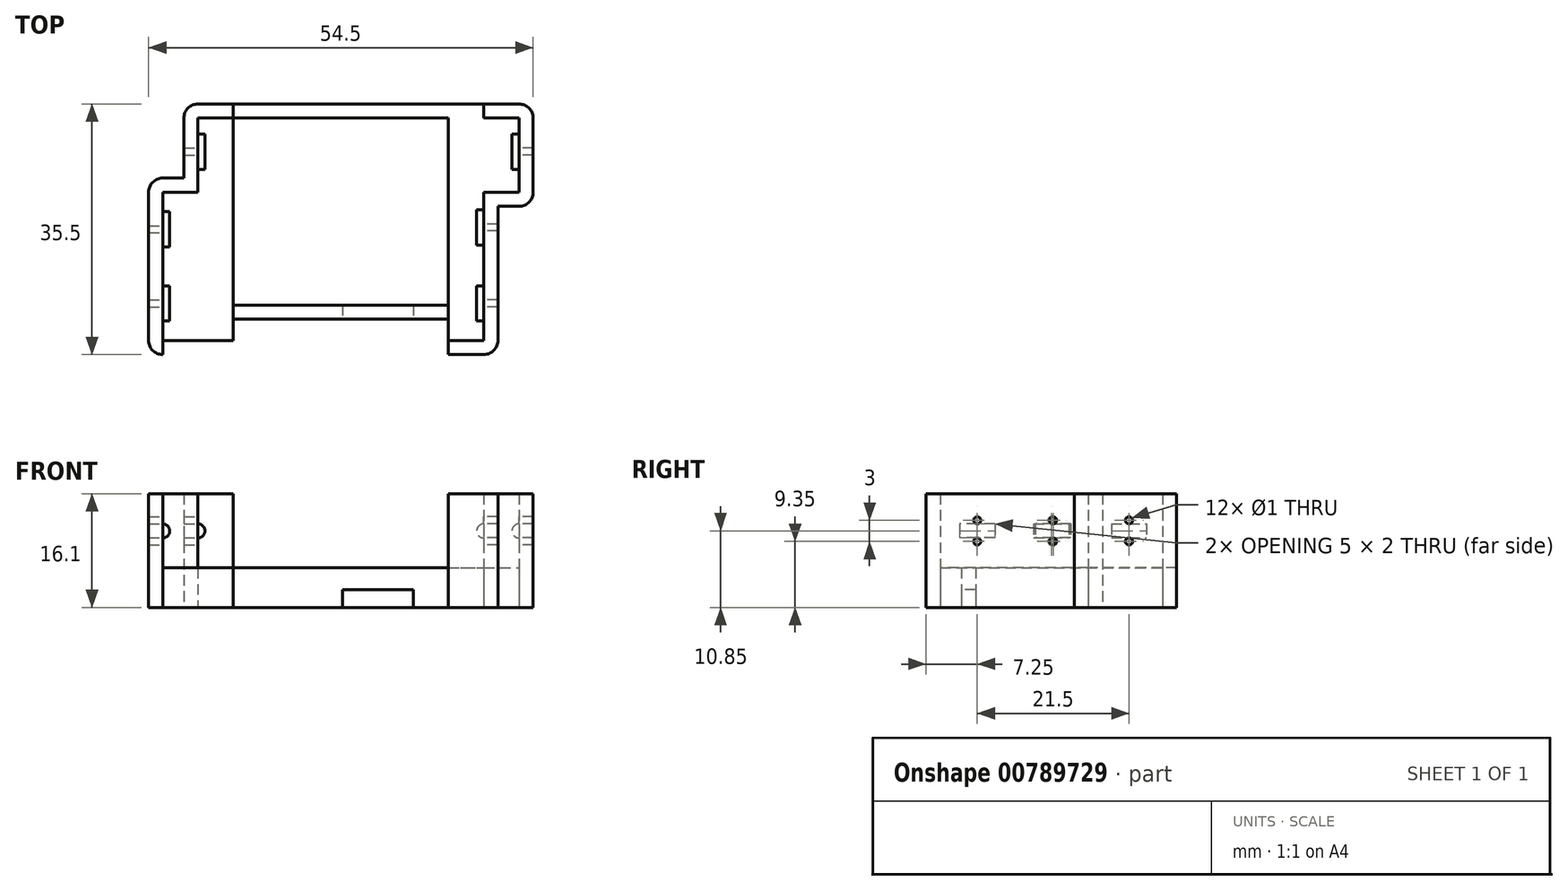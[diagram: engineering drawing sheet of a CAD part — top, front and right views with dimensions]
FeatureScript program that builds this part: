
annotation { "Feature Type Name" : "Feature", "Feature Type Description" : "" }
export const myFeature = defineFeature(function(context is Context, id is Id, definition is map)
    precondition{}
    {
        {
            var Q0;
            Q0=qCreatedBy(makeId("Top.planeOp"),FACE);
            var sketch = newSketch(context, id + "F0", { "sketchPlane" : qUnion([Q0])});
            skLineSegment(sketch, "E0", {"start": v(0, 0) * mm, "end": v(0, 23) * mm});
            skLineSegment(sketch, "E1", {"start": v(0, 23) * mm, "end": v(5, 23) * mm});
            skLineSegment(sketch, "E2", {"start": v(5, 23) * mm, "end": v(5, 35.5) * mm});
            skLineSegment(sketch, "E3", {"start": v(5, 35.5) * mm, "end": v(54.5, 35.5) * mm});
            skLineSegment(sketch, "E4", {"start": v(54.5, 35.5) * mm, "end": v(54.5, 23) * mm});
            skLineSegment(sketch, "E5", {"start": v(54.5, 23) * mm, "end": v(49.5, 23) * mm});
            skLineSegment(sketch, "E6", {"start": v(49.5, 23) * mm, "end": v(49.5, 0) * mm});
            skLineSegment(sketch, "E7", {"start": v(49.5, 0) * mm, "end": v(0, 0) * mm});
            skLineSegment(sketch, "E8", {"start": v(5, 33.5) * mm, "end": v(54.5, 33.5) * mm});
            skLineSegment(sketch, "E9", {"start": v(5, 23) * mm, "end": v(49.5, 23) * mm});
            skLineSegment(sketch, "E10", {"start": v(7, 35.5) * mm, "end": v(7, 0) * mm});
            skLineSegment(sketch, "E11", {"start": v(2, 0) * mm, "end": v(2, 23) * mm});
            skLineSegment(sketch, "E12", {"start": v(0, 2) * mm, "end": v(49.5, 2) * mm});
            skLineSegment(sketch, "E13", {"start": v(47.5, 23) * mm, "end": v(47.5, 0) * mm});
            skLineSegment(sketch, "E14", {"start": v(52.5, 35.5) * mm, "end": v(52.5, 23) * mm});
            skLineSegment(sketch, "E15", {"start": v(12, 35.5) * mm, "end": v(12, 0) * mm});
            skLineSegment(sketch, "E16", {"start": v(0, 23) * mm, "end": v(0, 25) * mm});
            skLineSegment(sketch, "E17", {"start": v(0, 25) * mm, "end": v(5, 25) * mm});
            skLineSegment(sketch, "E18", {"start": v(54.5, 23) * mm, "end": v(54.5, 21) * mm});
            skLineSegment(sketch, "E19", {"start": v(54.5, 21) * mm, "end": v(49.5, 21) * mm});
            skLineSegment(sketch, "E20", {"start": v(7, 0) * mm, "end": v(7, 2) * mm});
            skLineSegment(sketch, "E21", {"start": v(42.5, 0) * mm, "end": v(42.5, 35.5) * mm});
            skLineSegment(sketch, "E22", {"start": v(47.5, 35.5) * mm, "end": v(47.5, 33.5) * mm});
            skLineSegment(sketch, "E23", {"start": v(12, 5) * mm, "end": v(42.5, 5) * mm});
            skLineSegment(sketch, "E24", {"start": v(42.5, 7) * mm, "end": v(12, 7) * mm});
            skSolve(sketch);
        }
        {
            var Q0;
            {var subQ1=sQuery(id+"F0.wireOp",EDGE,"E4");var subQ3=sQuery(id+"F0.wireOp",EDGE,"E8");var subQ4=makeQuery(id+"F0.imprint","INTERSECT",VERTEX,{"derivedFrom":[subQ1,subQ3]});Q0=makeQuery(id+"F0.imprint","IMPRINT",FACE,{"disambiguationData":[TD([[makeQuery(id+"F0.imprint","IMPRINT",EDGE,{"disambiguationData":[TD([[subQ4,1.0]])],"derivedFrom":subQ3}),-1.0]])]});}
            var Q1;
            {var subQ0=sQuery(id+"F0.wireOp",EDGE,"E4");var subQ1=sQuery(id+"F0.wireOp",EDGE,"E3");var subQ2=makeQuery(id+"F0.imprint","INTERSECT",VERTEX,{"derivedFrom":[subQ1,subQ0]});Q1=makeQuery(id+"F0.imprint","IMPRINT",FACE,{"disambiguationData":[TD([[makeQuery(id+"F0.imprint","IMPRINT",EDGE,{"disambiguationData":[TD([[subQ2,1.0]])],"derivedFrom":subQ1}),-1.0]])]});}
            var Q2;
            {var subQ0=sQuery(id+"F0.wireOp",EDGE,"E18");Q2=makeQuery(id+"F0.imprint","IMPRINT",FACE,{"disambiguationData":[TD([[makeQuery(id+"F0.imprint","IMPRINT",EDGE,{"derivedFrom":subQ0}),-1.0]])]});}
            var Q3;
            {var subQ0=sQuery(id+"F0.wireOp",EDGE,"E12");var subQ1=sQuery(id+"F0.wireOp",EDGE,"E6");var subQ2=makeQuery(id+"F0.imprint","INTERSECT",VERTEX,{"derivedFrom":[subQ1,subQ0]});Q3=makeQuery(id+"F0.imprint","IMPRINT",FACE,{"disambiguationData":[TD([[makeQuery(id+"F0.imprint","IMPRINT",EDGE,{"disambiguationData":[TD([[subQ2,1.0]])],"derivedFrom":subQ1}),-1.0]])]});}
            var Q4;
            {var subQ0=sQuery(id+"F0.wireOp",EDGE,"E7");var subQ1=sQuery(id+"F0.wireOp",EDGE,"E6");var subQ2=makeQuery(id+"F0.imprint","INTERSECT",VERTEX,{"derivedFrom":[subQ1,subQ0]});Q4=makeQuery(id+"F0.imprint","IMPRINT",FACE,{"disambiguationData":[TD([[makeQuery(id+"F0.imprint","IMPRINT",EDGE,{"disambiguationData":[TD([[subQ2,1.0]])],"derivedFrom":subQ1}),-1.0]])]});}
            var Q5;
            {var subQ0=sQuery(id+"F0.wireOp",EDGE,"E3");var subQ1=sQuery(id+"F0.wireOp",EDGE,"E2");var subQ2=makeQuery(id+"F0.imprint","INTERSECT",VERTEX,{"derivedFrom":[subQ1,subQ0]});Q5=makeQuery(id+"F0.imprint","IMPRINT",FACE,{"disambiguationData":[TD([[makeQuery(id+"F0.imprint","IMPRINT",EDGE,{"disambiguationData":[TD([[subQ2,1.0]])],"derivedFrom":subQ1}),-1.0]])]});}
            var Q6;
            {var subQ1=sQuery(id+"F0.wireOp",EDGE,"E2");var subQ5=sQuery(id+"F0.wireOp",EDGE,"E8");var subQ6=makeQuery(id+"F0.imprint","INTERSECT",VERTEX,{"derivedFrom":[subQ1,subQ5]});Q6=makeQuery(id+"F0.imprint","IMPRINT",FACE,{"disambiguationData":[TD([[makeQuery(id+"F0.imprint","IMPRINT",EDGE,{"disambiguationData":[TD([[subQ6,1.0]])],"derivedFrom":subQ1}),-1.0]])]});}
            var Q7;
            {var subQ0=sQuery(id+"F0.wireOp",EDGE,"E16");Q7=makeQuery(id+"F0.imprint","IMPRINT",FACE,{"disambiguationData":[TD([[makeQuery(id+"F0.imprint","IMPRINT",EDGE,{"derivedFrom":subQ0}),-1.0]])]});}
            var Q8;
            {var subQ0=sQuery(id+"F0.wireOp",EDGE,"E1");var subQ5=sQuery(id+"F0.wireOp",EDGE,"E11");var subQ6=makeQuery(id+"F0.imprint","INTERSECT",VERTEX,{"derivedFrom":[subQ0,subQ5]});Q8=makeQuery(id+"F0.imprint","IMPRINT",FACE,{"disambiguationData":[TD([[makeQuery(id+"F0.imprint","IMPRINT",EDGE,{"disambiguationData":[TD([[subQ6,1.0]])],"derivedFrom":subQ5}),1.0]])]});}
            var Q9;
            {var subQ0=sQuery(id+"F0.wireOp",EDGE,"E7");var subQ1=sQuery(id+"F0.wireOp",EDGE,"E0");var subQ2=makeQuery(id+"F0.imprint","INTERSECT",VERTEX,{"derivedFrom":[subQ1,subQ0]});Q9=makeQuery(id+"F0.imprint","IMPRINT",FACE,{"disambiguationData":[TD([[makeQuery(id+"F0.imprint","IMPRINT",EDGE,{"disambiguationData":[TD([[subQ2,-1.0]])],"derivedFrom":subQ1}),-1.0]])]});}
            var Q10;
            {var subQ3=sQuery(id+"F0.wireOp",EDGE,"E20");Q10=makeQuery(id+"F0.imprint","IMPRINT",FACE,{"disambiguationData":[TD([[makeQuery(id+"F0.imprint","IMPRINT",EDGE,{"derivedFrom":subQ3}),1.0]])]});}
            var Q11;
            {var subQ0=sQuery(id+"F0.wireOp",EDGE,"E13");var subQ1=sQuery(id+"F0.wireOp",EDGE,"E7");var subQ2=makeQuery(id+"F0.imprint","INTERSECT",VERTEX,{"derivedFrom":[subQ1,subQ0]});Q11=makeQuery(id+"F0.imprint","IMPRINT",FACE,{"disambiguationData":[TD([[makeQuery(id+"F0.imprint","IMPRINT",EDGE,{"disambiguationData":[TD([[subQ2,-1.0]])],"derivedFrom":subQ1}),-1.0]])]});}
            var Q12;
            {var subQ0=sQuery(id+"F0.wireOp",EDGE,"E10");var subQ1=sQuery(id+"F0.wireOp",EDGE,"E3");var subQ2=makeQuery(id+"F0.imprint","INTERSECT",VERTEX,{"derivedFrom":[subQ1,subQ0]});Q12=makeQuery(id+"F0.imprint","IMPRINT",FACE,{"disambiguationData":[TD([[makeQuery(id+"F0.imprint","IMPRINT",EDGE,{"disambiguationData":[TD([[subQ2,-1.0]])],"derivedFrom":subQ1}),-1.0]])]});}
            var Q13;
            {var subQ3=sQuery(id+"F0.wireOp",EDGE,"E22");Q13=makeQuery(id+"F0.imprint","IMPRINT",FACE,{"disambiguationData":[TD([[makeQuery(id+"F0.imprint","IMPRINT",EDGE,{"derivedFrom":subQ3}),1.0]])]});}
            extrude(context, id + "F1", {"entities" : qUnion([Q0, Q1, Q2, Q3, Q4, Q5, Q6, Q7, Q8, Q9, Q10, Q11, Q12, Q13]), "depth" : 16.1 * mm, "offsetDistance" : 25 * mm});
        }
        {
            var Q0;
            {var subQ0=sQuery(id+"F0.wireOp",EDGE,"E15");var subQ1=sQuery(id+"F0.wireOp",EDGE,"E3");var subQ2=makeQuery(id+"F0.imprint","INTERSECT",VERTEX,{"derivedFrom":[subQ1,subQ0]});Q0=makeQuery(id+"F0.imprint","IMPRINT",FACE,{"disambiguationData":[TD([[makeQuery(id+"F0.imprint","IMPRINT",EDGE,{"disambiguationData":[TD([[subQ2,-1.0]])],"derivedFrom":subQ1}),-1.0]])]});}
            var Q1;
            {var subQ3=sQuery(id+"F0.wireOp",EDGE,"E22");Q1=makeQuery(id+"F0.imprint","IMPRINT",FACE,{"disambiguationData":[TD([[makeQuery(id+"F0.imprint","IMPRINT",EDGE,{"derivedFrom":subQ3}),-1.0]])]});}
            var Q2;
            {var subQ3=sQuery(id+"F0.wireOp",EDGE,"E20");Q2=makeQuery(id+"F0.imprint","IMPRINT",FACE,{"disambiguationData":[TD([[makeQuery(id+"F0.imprint","IMPRINT",EDGE,{"derivedFrom":subQ3}),-1.0]])]});}
            var Q3;
            {var subQ0=sQuery(id+"F0.wireOp",EDGE,"E11");var subQ1=sQuery(id+"F0.wireOp",EDGE,"E1");var subQ2=makeQuery(id+"F0.imprint","INTERSECT",VERTEX,{"derivedFrom":[subQ1,subQ0]});Q3=makeQuery(id+"F0.imprint","IMPRINT",FACE,{"disambiguationData":[TD([[makeQuery(id+"F0.imprint","IMPRINT",EDGE,{"disambiguationData":[TD([[subQ2,1.0]])],"derivedFrom":subQ0}),-1.0]])]});}
            var Q4;
            {var subQ0=sQuery(id+"F0.wireOp",EDGE,"E10");var subQ1=sQuery(id+"F0.wireOp",EDGE,"E9");var subQ2=makeQuery(id+"F0.imprint","INTERSECT",VERTEX,{"derivedFrom":[subQ1,subQ0]});Q4=makeQuery(id+"F0.imprint","IMPRINT",FACE,{"disambiguationData":[TD([[makeQuery(id+"F0.imprint","IMPRINT",EDGE,{"disambiguationData":[TD([[subQ2,-1.0]])],"derivedFrom":subQ1}),-1.0]])]});}
            var Q5;
            {var subQ0=sQuery(id+"F0.wireOp",EDGE,"E10");var subQ1=sQuery(id+"F0.wireOp",EDGE,"E8");var subQ2=makeQuery(id+"F0.imprint","INTERSECT",VERTEX,{"derivedFrom":[subQ1,subQ0]});Q5=makeQuery(id+"F0.imprint","IMPRINT",FACE,{"disambiguationData":[TD([[makeQuery(id+"F0.imprint","IMPRINT",EDGE,{"disambiguationData":[TD([[subQ2,-1.0]])],"derivedFrom":subQ1}),-1.0]])]});}
            var Q6;
            {var subQ4=sQuery(id+"F0.wireOp",EDGE,"E8");var subQ5=makeQuery(id+"F0.imprint","INTERSECT",VERTEX,{"derivedFrom":[subQ4,sQuery(id+"F0.wireOp",EDGE,"E22")]});Q6=makeQuery(id+"F0.imprint","IMPRINT",FACE,{"disambiguationData":[TD([[makeQuery(id+"F0.imprint","IMPRINT",EDGE,{"disambiguationData":[TD([[subQ5,1.0]])],"derivedFrom":subQ4}),-1.0]])]});}
            var Q7;
            {var subQ0=sQuery(id+"F0.wireOp",EDGE,"E13");var subQ1=sQuery(id+"F0.wireOp",EDGE,"E9");var subQ2=makeQuery(id+"F0.imprint","INTERSECT",VERTEX,{"derivedFrom":[subQ1,subQ0]});Q7=makeQuery(id+"F0.imprint","IMPRINT",FACE,{"disambiguationData":[TD([[makeQuery(id+"F0.imprint","IMPRINT",EDGE,{"disambiguationData":[TD([[subQ2,1.0]])],"derivedFrom":subQ1}),-1.0]])]});}
            extrude(context, id + "F2", {"entities" : qUnion([Q0, Q1, Q2, Q3, Q4, Q5, Q6, Q7]), "depth" : 5.6 * mm, "offsetDistance" : 25 * mm});
        }
        {
            var Q0;
            {var subQ0=sQuery(id+"F0.wireOp",EDGE,"E23");Q0=makeQuery(id+"F0.imprint","IMPRINT",FACE,{"disambiguationData":[TD([[makeQuery(id+"F0.imprint","IMPRINT",EDGE,{"derivedFrom":subQ0}),1.0]])]});}
            extrude(context, id + "F3", {"entities" : qUnion([Q0]), "depth" : 5.6 * mm, "offsetDistance" : 25 * mm});
        }
        {
            var Q0;
            Q0=makeQuery(id+"F1.opExtrude","SWEPT_EDGE",EDGE,{"disambiguationData":[OSD([sQuery(id+"F0.wireOp",EDGE,"E0"),sQuery(id+"F0.wireOp",EDGE,"E7")])]});
            var Q1;
            Q1=makeQuery(id+"F1.opExtrude","SWEPT_EDGE",EDGE,{"disambiguationData":[OSD([sQuery(id+"F0.wireOp",EDGE,"E16"),sQuery(id+"F0.wireOp",EDGE,"E17")])]});
            var Q2;
            Q2=makeQuery(id+"F1.opExtrude","SWEPT_EDGE",EDGE,{"disambiguationData":[OSD([sQuery(id+"F0.wireOp",EDGE,"E2"),sQuery(id+"F0.wireOp",EDGE,"E3")])]});
            var Q3;
            Q3=makeQuery(id+"F1.opExtrude","SWEPT_EDGE",EDGE,{"disambiguationData":[OSD([sQuery(id+"F0.wireOp",EDGE,"E3"),sQuery(id+"F0.wireOp",EDGE,"E4")])]});
            var Q4;
            Q4=makeQuery(id+"F1.opExtrude","SWEPT_EDGE",EDGE,{"disambiguationData":[OSD([sQuery(id+"F0.wireOp",EDGE,"E18"),sQuery(id+"F0.wireOp",EDGE,"E19")])]});
            var Q5;
            Q5=makeQuery(id+"F1.opExtrude","SWEPT_EDGE",EDGE,{"disambiguationData":[OSD([sQuery(id+"F0.wireOp",EDGE,"E6"),sQuery(id+"F0.wireOp",EDGE,"E7")])]});
            fillet(context, id + "F4", {"entities" : qUnion([Q0, Q1, Q2, Q3, Q4, Q5]), "radius" : 2 * mm, "tangentPropagation" : true, "allowEdgeOverflow" : false});
        }
        {
            var Q0;
            Q0=makeQuery(id+"F1.opExtrude","SWEPT_EDGE",EDGE,{"disambiguationData":[OSD([sQuery(id+"F0.wireOp",EDGE,"E9"),sQuery(id+"F0.wireOp",EDGE,"E13")])]});
            cPoint(context, id + "F5", {"entities" : qUnion([Q0]), "parameter" : 0.5});
        }
        {
            var Q0;
            Q0=makeQuery(id+"F1.opExtrude","CAP_EDGE",EDGE,{"disambiguationData":[OSD([sQuery(id+"F0.wireOp",EDGE,"E13")])],"isStart":false});
            cPoint(context, id + "F6", {"entities" : qUnion([Q0]), "parameter" : 0.5});
        }
        {
            var Q0;
            Q0=makeQuery(id+"F2.opExtrude","CAP_EDGE",EDGE,{"disambiguationData":[OSD([sQuery(id+"F0.wireOp",EDGE,"E13")])],"isStart":false});
            cPoint(context, id + "F7", {"entities" : qUnion([Q0]), "parameter" : 0.5});
        }
        {
            var Q0;
            Q0 = qCreatedBy(id + "F5" ,VERTEX);
            var Q1;
            Q1 = qCreatedBy(id + "F6" ,VERTEX);
            var Q2;
            Q2 = qCreatedBy(id + "F7" ,VERTEX);
            cPlane(context, id + "F8", {"entities" : qUnion([Q0, Q1, Q2]), "cplaneType" : CPlaneType.THREE_POINT, "offset" : 25 * mm, "width" : 150 * mm, "height" : 150 * mm});
        }
        {
            var Q0;
            Q0=makeQuery(id+"F2.opExtrude","CAP_EDGE",EDGE,{"disambiguationData":[OSD([sQuery(id+"F0.wireOp",EDGE,"E14")])],"isStart":false});
            cPoint(context, id + "F9", {"entities" : qUnion([Q0]), "parameter" : 0.5});
        }
        {
            var Q0;
            Q0=makeQuery(id+"F1.opExtrude","CAP_VERTEX",VERTEX,{"disambiguationData":[OSD([sQuery(id+"F0.wireOp",EDGE,"E8"),sQuery(id+"F0.wireOp",EDGE,"E14")])],"isStart":false});
            var Q1;
            Q1=makeQuery(id+"F2.opExtrude","CAP_VERTEX",VERTEX,{"disambiguationData":[OSD([sQuery(id+"F0.wireOp",EDGE,"E8"),sQuery(id+"F0.wireOp",EDGE,"E14")])],"isStart":false});
            var Q2;
            Q2 = qCreatedBy(id + "F9" ,VERTEX);
            cPlane(context, id + "F10", {"entities" : qUnion([Q0, Q1, Q2]), "cplaneType" : CPlaneType.THREE_POINT, "offset" : 25 * mm, "width" : 150 * mm, "height" : 150 * mm});
        }
        {
            var Q0;
            Q0=makeQuery(id+"F1.opExtrude","CAP_EDGE",EDGE,{"disambiguationData":[OSD([sQuery(id+"F0.wireOp",EDGE,"E11")])],"isStart":false});
            cPoint(context, id + "F11", {"entities" : qUnion([Q0]), "parameter" : 0.5});
        }
        {
            var Q0;
            Q0=makeQuery(id+"F1.opExtrude","SWEPT_EDGE",EDGE,{"disambiguationData":[OSD([sQuery(id+"F0.wireOp",EDGE,"E1"),sQuery(id+"F0.wireOp",EDGE,"E11")])]});
            cPoint(context, id + "F12", {"entities" : qUnion([Q0]), "parameter" : 0.5});
        }
        {
            var Q0;
            Q0=makeQuery(id+"F2.opExtrude","CAP_EDGE",EDGE,{"disambiguationData":[OSD([sQuery(id+"F0.wireOp",EDGE,"E11")])],"isStart":false});
            cPoint(context, id + "F13", {"entities" : qUnion([Q0]), "parameter" : 0.5});
        }
        {
            var Q0;
            Q0 = qCreatedBy(id + "F11" ,VERTEX);
            var Q1;
            Q1 = qCreatedBy(id + "F12" ,VERTEX);
            var Q2;
            Q2 = qCreatedBy(id + "F13" ,VERTEX);
            cPlane(context, id + "F14", {"entities" : qUnion([Q0, Q1, Q2]), "cplaneType" : CPlaneType.THREE_POINT, "offset" : 25 * mm, "width" : 150 * mm, "height" : 150 * mm});
        }
        {
            var Q0;
            Q0=makeQuery(id+"F1.opExtrude","CAP_EDGE",EDGE,{"disambiguationData":[OSD([sQuery(id+"F0.wireOp",EDGE,"E10")])],"isStart":false});
            cPoint(context, id + "F15", {"entities" : qUnion([Q0]), "parameter" : 0.5});
        }
        {
            var Q0;
            Q0=makeQuery(id+"F2.opExtrude","CAP_EDGE",EDGE,{"disambiguationData":[OSD([sQuery(id+"F0.wireOp",EDGE,"E10")])],"isStart":false});
            cPoint(context, id + "F16", {"entities" : qUnion([Q0]), "parameter" : 0.5});
        }
        {
            var Q0;
            Q0 = qCreatedBy(id + "F15" ,VERTEX);
            var Q1;
            Q1 = qCreatedBy(id + "F16" ,VERTEX);
            var Q2;
            Q2=makeQuery(id+"F1.opExtrude","CAP_VERTEX",VERTEX,{"disambiguationData":[OSD([sQuery(id+"F0.wireOp",EDGE,"E9"),sQuery(id+"F0.wireOp",EDGE,"E10")])],"isStart":false});
            cPlane(context, id + "F17", {"entities" : qUnion([Q0, Q1, Q2]), "cplaneType" : CPlaneType.THREE_POINT, "offset" : 25 * mm, "width" : 150 * mm, "height" : 150 * mm});
        }
        {
            var Q0;
            Q0=qCreatedBy(id+"F14.planeOp",FACE);
            var sketch = newSketch(context, id + "F18", { "sketchPlane" : qUnion([Q0])});
            skLineSegment(sketch, "E25.bottom", {"start": v(2, 16.1) * mm, "end": v(33.5, 16.1) * mm});
            skLineSegment(sketch, "E25.top", {"start": v(2, 5.6) * mm, "end": v(33.5, 5.6) * mm});
            skLineSegment(sketch, "E25.left", {"start": v(2, 16.1) * mm, "end": v(2, 5.6) * mm});
            skLineSegment(sketch, "E25.right", {"start": v(33.5, 16.1) * mm, "end": v(33.5, 5.6) * mm});
            skLineSegment(sketch, "E26.bottom", {"start": v(4.75, 9.85) * mm, "end": v(9.75, 9.85) * mm});
            skLineSegment(sketch, "E26.top", {"start": v(4.75, 11.85) * mm, "end": v(9.75, 11.85) * mm});
            skLineSegment(sketch, "E26.left", {"start": v(4.75, 11.85) * mm, "end": v(4.75, 9.85) * mm});
            skLineSegment(sketch, "E26.right", {"start": v(9.75, 11.85) * mm, "end": v(9.75, 9.85) * mm});
            skLineSegment(sketch, "E27.bottom", {"start": v(15.25, 9.85) * mm, "end": v(20.25, 9.85) * mm});
            skLineSegment(sketch, "E27.top", {"start": v(15.25, 11.85) * mm, "end": v(20.25, 11.85) * mm});
            skLineSegment(sketch, "E27.left", {"start": v(15.25, 11.85) * mm, "end": v(15.25, 9.85) * mm});
            skLineSegment(sketch, "E27.right", {"start": v(20.25, 11.85) * mm, "end": v(20.25, 9.85) * mm});
            skLineSegment(sketch, "E28.bottom", {"start": v(25.75, 9.85) * mm, "end": v(30.75, 9.85) * mm});
            skLineSegment(sketch, "E28.top", {"start": v(25.75, 11.85) * mm, "end": v(30.75, 11.85) * mm});
            skLineSegment(sketch, "E28.left", {"start": v(25.75, 11.85) * mm, "end": v(25.75, 9.85) * mm});
            skLineSegment(sketch, "E28.right", {"start": v(30.75, 11.85) * mm, "end": v(30.75, 9.85) * mm});
            skLineSegment(sketch, "E29", {"start": v(30.75, 10.85) * mm, "end": v(33.5, 10.85) * mm, "construction": true});
            skLineSegment(sketch, "E30", {"start": v(4.75, 10.85) * mm, "end": v(2, 10.85) * mm, "construction": true});
            skLineSegment(sketch, "E31", {"start": v(9.75, 10.85) * mm, "end": v(15.25, 10.85) * mm, "construction": true});
            skLineSegment(sketch, "E32", {"start": v(20.25, 10.85) * mm, "end": v(25.75, 10.85) * mm, "construction": true});
            skCircle(sketch, "E33", {"center": v(28.25, 12.35) * mm, "radius": 0.5 * mm});
            skPoint(sketch, "E33.centerSnap0", {"position": v(28.25, 11.85) * mm});
            skCircle(sketch, "E34", {"center": v(17.75, 12.35) * mm, "radius": 0.5 * mm});
            skCircle(sketch, "E35", {"center": v(7.25, 12.35) * mm, "radius": 0.5 * mm});
            skPoint(sketch, "E35.centerSnap0", {"position": v(7.25, 11.85) * mm});
            skCircle(sketch, "E36", {"center": v(7.25, 9.35) * mm, "radius": 0.5 * mm});
            skPoint(sketch, "E36.centerSnap0", {"position": v(7.25, 9.85) * mm});
            skCircle(sketch, "E37", {"center": v(17.75, 9.35) * mm, "radius": 0.5 * mm});
            skPoint(sketch, "E37.centerSnap0", {"position": v(17.75, 9.85) * mm});
            skCircle(sketch, "E38", {"center": v(28.25, 9.35) * mm, "radius": 0.5 * mm});
            skPoint(sketch, "E38.centerSnap0", {"position": v(28.25, 9.85) * mm});
            skSolve(sketch);
        }
        {
            var Q0;
            Q0=qCreatedBy(id+"F17.planeOp",FACE);
            var sketch = newSketch(context, id + "F19", { "sketchPlane" : qUnion([Q0])});
            skLineSegment(sketch, "E39.bottom", {"start": v(2, 16.1) * mm, "end": v(34, 16.1) * mm});
            skLineSegment(sketch, "E39.top", {"start": v(2, 5.6) * mm, "end": v(34, 5.6) * mm});
            skLineSegment(sketch, "E39.left", {"start": v(2, 16.1) * mm, "end": v(2, 5.6) * mm});
            skLineSegment(sketch, "E39.right", {"start": v(34, 16.1) * mm, "end": v(34, 5.6) * mm});
            skLineSegment(sketch, "E40.bottom", {"start": v(4.75, 9.85) * mm, "end": v(9.75, 9.85) * mm});
            skLineSegment(sketch, "E40.top", {"start": v(4.75, 11.85) * mm, "end": v(9.75, 11.85) * mm});
            skLineSegment(sketch, "E40.left", {"start": v(4.75, 11.85) * mm, "end": v(4.75, 9.85) * mm});
            skLineSegment(sketch, "E40.right", {"start": v(9.75, 11.85) * mm, "end": v(9.75, 9.85) * mm});
            skLineSegment(sketch, "E41.bottom", {"start": v(15.5, 9.85) * mm, "end": v(20.5, 9.85) * mm});
            skLineSegment(sketch, "E41.top", {"start": v(15.5, 11.85) * mm, "end": v(20.5, 11.85) * mm});
            skLineSegment(sketch, "E41.left", {"start": v(15.5, 11.85) * mm, "end": v(15.5, 9.85) * mm});
            skLineSegment(sketch, "E41.right", {"start": v(20.5, 11.85) * mm, "end": v(20.5, 9.85) * mm});
            skLineSegment(sketch, "E42.bottom", {"start": v(26.25, 9.85) * mm, "end": v(31.25, 9.85) * mm});
            skLineSegment(sketch, "E42.top", {"start": v(26.25, 11.85) * mm, "end": v(31.25, 11.85) * mm});
            skLineSegment(sketch, "E42.left", {"start": v(26.25, 11.85) * mm, "end": v(26.25, 9.85) * mm});
            skLineSegment(sketch, "E42.right", {"start": v(31.25, 11.85) * mm, "end": v(31.25, 9.85) * mm});
            skLineSegment(sketch, "E43", {"start": v(31.25, 10.85) * mm, "end": v(34, 10.85) * mm, "construction": true});
            skLineSegment(sketch, "E44", {"start": v(4.75, 10.85) * mm, "end": v(2, 10.85) * mm, "construction": true});
            skLineSegment(sketch, "E45", {"start": v(9.75, 10.85) * mm, "end": v(15.5, 10.85) * mm, "construction": true});
            skLineSegment(sketch, "E46", {"start": v(20.5, 10.85) * mm, "end": v(26.25, 10.85) * mm, "construction": true});
            skCircle(sketch, "E47", {"center": v(28.75, 12.35) * mm, "radius": 0.5 * mm});
            skPoint(sketch, "E47.centerSnap0", {"position": v(28.75, 11.85) * mm});
            skCircle(sketch, "E48", {"center": v(18, 12.35) * mm, "radius": 0.5 * mm});
            skCircle(sketch, "E49", {"center": v(7.25, 12.35) * mm, "radius": 0.5 * mm});
            skPoint(sketch, "E49.centerSnap0", {"position": v(7.25, 11.85) * mm});
            skCircle(sketch, "E50", {"center": v(7.25, 9.35) * mm, "radius": 0.5 * mm});
            skPoint(sketch, "E50.centerSnap0", {"position": v(7.25, 9.85) * mm});
            skCircle(sketch, "E51", {"center": v(18, 9.35) * mm, "radius": 0.5 * mm});
            skPoint(sketch, "E51.centerSnap0", {"position": v(18, 9.85) * mm});
            skCircle(sketch, "E52", {"center": v(28.75, 9.35) * mm, "radius": 0.5 * mm});
            skPoint(sketch, "E52.centerSnap0", {"position": v(28.75, 9.85) * mm});
            skSolve(sketch);
        }
        {
            var Q0;
            Q0=qCreatedBy(id+"F8.planeOp",FACE);
            var sketch = newSketch(context, id + "F20", { "sketchPlane" : qUnion([Q0])});
            skLineSegment(sketch, "E53.bottom", {"start": v(-34, 16.1) * mm, "end": v(-2, 16.1) * mm});
            skLineSegment(sketch, "E53.top", {"start": v(-34, 5.6) * mm, "end": v(-2, 5.6) * mm});
            skLineSegment(sketch, "E53.left", {"start": v(-34, 16.1) * mm, "end": v(-34, 5.6) * mm});
            skLineSegment(sketch, "E53.right", {"start": v(-2, 16.1) * mm, "end": v(-2, 5.6) * mm});
            skLineSegment(sketch, "E54.bottom", {"start": v(-31.25, 9.85) * mm, "end": v(-26.25, 9.85) * mm});
            skLineSegment(sketch, "E54.top", {"start": v(-31.25, 11.85) * mm, "end": v(-26.25, 11.85) * mm});
            skLineSegment(sketch, "E54.left", {"start": v(-31.25, 11.85) * mm, "end": v(-31.25, 9.85) * mm});
            skLineSegment(sketch, "E54.right", {"start": v(-26.25, 11.85) * mm, "end": v(-26.25, 9.85) * mm});
            skLineSegment(sketch, "E55.bottom", {"start": v(-20.5, 9.85) * mm, "end": v(-15.5, 9.85) * mm});
            skLineSegment(sketch, "E55.top", {"start": v(-20.5, 11.85) * mm, "end": v(-15.5, 11.85) * mm});
            skLineSegment(sketch, "E55.left", {"start": v(-20.5, 11.85) * mm, "end": v(-20.5, 9.85) * mm});
            skLineSegment(sketch, "E55.right", {"start": v(-15.5, 11.85) * mm, "end": v(-15.5, 9.85) * mm});
            skLineSegment(sketch, "E56.bottom", {"start": v(-9.75, 9.85) * mm, "end": v(-4.75, 9.85) * mm});
            skLineSegment(sketch, "E56.top", {"start": v(-9.75, 11.85) * mm, "end": v(-4.75, 11.85) * mm});
            skLineSegment(sketch, "E56.left", {"start": v(-9.75, 11.85) * mm, "end": v(-9.75, 9.85) * mm});
            skLineSegment(sketch, "E56.right", {"start": v(-4.75, 11.85) * mm, "end": v(-4.75, 9.85) * mm});
            skLineSegment(sketch, "E57", {"start": v(-4.75, 10.85) * mm, "end": v(-2, 10.85) * mm, "construction": true});
            skLineSegment(sketch, "E58", {"start": v(-31.25, 10.85) * mm, "end": v(-34, 10.85) * mm, "construction": true});
            skLineSegment(sketch, "E59", {"start": v(-26.25, 10.85) * mm, "end": v(-20.5, 10.85) * mm, "construction": true});
            skLineSegment(sketch, "E60", {"start": v(-15.5, 10.85) * mm, "end": v(-9.75, 10.85) * mm, "construction": true});
            skCircle(sketch, "E61", {"center": v(-7.25, 12.35) * mm, "radius": 0.5 * mm});
            skPoint(sketch, "E61.centerSnap0", {"position": v(-7.25, 11.85) * mm});
            skCircle(sketch, "E62", {"center": v(-18, 12.35) * mm, "radius": 0.5 * mm});
            skCircle(sketch, "E63", {"center": v(-28.75, 12.35) * mm, "radius": 0.5 * mm});
            skPoint(sketch, "E63.centerSnap0", {"position": v(-28.75, 11.85) * mm});
            skCircle(sketch, "E64", {"center": v(-28.75, 9.35) * mm, "radius": 0.5 * mm});
            skPoint(sketch, "E64.centerSnap0", {"position": v(-28.75, 9.85) * mm});
            skCircle(sketch, "E65", {"center": v(-18, 9.35) * mm, "radius": 0.5 * mm});
            skPoint(sketch, "E65.centerSnap0", {"position": v(-18, 9.85) * mm});
            skCircle(sketch, "E66", {"center": v(-7.25, 9.35) * mm, "radius": 0.5 * mm});
            skPoint(sketch, "E66.centerSnap0", {"position": v(-7.25, 9.85) * mm});
            skSolve(sketch);
        }
        {
            var Q0;
            Q0=qCreatedBy(id+"F10.planeOp",FACE);
            var sketch = newSketch(context, id + "F21", { "sketchPlane" : qUnion([Q0])});
            skLineSegment(sketch, "E67.bottom", {"start": v(2, 16.1) * mm, "end": v(34, 16.1) * mm});
            skLineSegment(sketch, "E67.top", {"start": v(2, 5.6) * mm, "end": v(34, 5.6) * mm});
            skLineSegment(sketch, "E67.left", {"start": v(2, 16.1) * mm, "end": v(2, 5.6) * mm});
            skLineSegment(sketch, "E67.right", {"start": v(34, 16.1) * mm, "end": v(34, 5.6) * mm});
            skLineSegment(sketch, "E68.bottom", {"start": v(4.75, 9.85) * mm, "end": v(9.75, 9.85) * mm});
            skLineSegment(sketch, "E68.top", {"start": v(4.75, 11.85) * mm, "end": v(9.75, 11.85) * mm});
            skLineSegment(sketch, "E68.left", {"start": v(4.75, 11.85) * mm, "end": v(4.75, 9.85) * mm});
            skLineSegment(sketch, "E68.right", {"start": v(9.75, 11.85) * mm, "end": v(9.75, 9.85) * mm});
            skLineSegment(sketch, "E69.bottom", {"start": v(15.5, 9.85) * mm, "end": v(20.5, 9.85) * mm});
            skLineSegment(sketch, "E69.top", {"start": v(15.5, 11.85) * mm, "end": v(20.5, 11.85) * mm});
            skLineSegment(sketch, "E69.left", {"start": v(15.5, 11.85) * mm, "end": v(15.5, 9.85) * mm});
            skLineSegment(sketch, "E69.right", {"start": v(20.5, 11.85) * mm, "end": v(20.5, 9.85) * mm});
            skLineSegment(sketch, "E70.bottom", {"start": v(26.25, 9.85) * mm, "end": v(31.25, 9.85) * mm});
            skLineSegment(sketch, "E70.top", {"start": v(26.25, 11.85) * mm, "end": v(31.25, 11.85) * mm});
            skLineSegment(sketch, "E70.left", {"start": v(26.25, 11.85) * mm, "end": v(26.25, 9.85) * mm});
            skLineSegment(sketch, "E70.right", {"start": v(31.25, 11.85) * mm, "end": v(31.25, 9.85) * mm});
            skLineSegment(sketch, "E71", {"start": v(31.25, 10.85) * mm, "end": v(34, 10.85) * mm, "construction": true});
            skLineSegment(sketch, "E72", {"start": v(4.75, 10.85) * mm, "end": v(2, 10.85) * mm, "construction": true});
            skLineSegment(sketch, "E73", {"start": v(9.75, 10.85) * mm, "end": v(15.5, 10.85) * mm, "construction": true});
            skLineSegment(sketch, "E74", {"start": v(20.5, 10.85) * mm, "end": v(26.25, 10.85) * mm, "construction": true});
            skCircle(sketch, "E75", {"center": v(28.75, 12.35) * mm, "radius": 0.5 * mm});
            skPoint(sketch, "E75.centerSnap0", {"position": v(28.75, 11.85) * mm});
            skCircle(sketch, "E76", {"center": v(18, 12.35) * mm, "radius": 0.5 * mm});
            skCircle(sketch, "E77", {"center": v(7.25, 12.35) * mm, "radius": 0.5 * mm});
            skPoint(sketch, "E77.centerSnap0", {"position": v(7.25, 11.85) * mm});
            skCircle(sketch, "E78", {"center": v(7.25, 9.35) * mm, "radius": 0.5 * mm});
            skPoint(sketch, "E78.centerSnap0", {"position": v(7.25, 9.85) * mm});
            skCircle(sketch, "E79", {"center": v(18, 9.35) * mm, "radius": 0.5 * mm});
            skPoint(sketch, "E79.centerSnap0", {"position": v(18, 9.85) * mm});
            skCircle(sketch, "E80", {"center": v(28.75, 9.35) * mm, "radius": 0.5 * mm});
            skPoint(sketch, "E80.centerSnap0", {"position": v(28.75, 9.85) * mm});
            skSolve(sketch);
        }
        {
            var Q0;
            {var subQ3=sQuery(id+"F18.wireOp",EDGE,"E26.left");Q0=makeQuery(id+"F18.imprint","IMPRINT",FACE,{"disambiguationData":[TD([[makeQuery(id+"F18.imprint","IMPRINT",EDGE,{"derivedFrom":subQ3}),1.0]])]});}
            var Q1;
            {var subQ3=sQuery(id+"F18.wireOp",EDGE,"E27.left");Q1=makeQuery(id+"F18.imprint","IMPRINT",FACE,{"disambiguationData":[TD([[makeQuery(id+"F18.imprint","IMPRINT",EDGE,{"derivedFrom":subQ3}),1.0]])]});}
            var Q2;
            {var subQ3=sQuery(id+"F19.wireOp",EDGE,"E42.left");Q2=makeQuery(id+"F19.imprint","IMPRINT",FACE,{"disambiguationData":[TD([[makeQuery(id+"F19.imprint","IMPRINT",EDGE,{"derivedFrom":subQ3}),1.0]])]});}
            extrude(context, id + "F22", {"entities" : qUnion([Q0, Q1, Q2]), "operationType" : NewBodyOperationType.ADD, "depth" : 1 * mm, "offsetDistance" : 25 * mm});
        }
        {
            var Q0;
            Q0=makeQuery(id+"F18.imprint","IMPRINT",FACE,{"disambiguationData":[TD([[makeQuery(id+"F18.imprint","IMPRINT",EDGE,{"derivedFrom":sQuery(id+"F18.wireOp",EDGE,"E34")}),1.0]])]});
            var Q1;
            Q1=makeQuery(id+"F18.imprint","IMPRINT",FACE,{"disambiguationData":[TD([[makeQuery(id+"F18.imprint","IMPRINT",EDGE,{"derivedFrom":sQuery(id+"F18.wireOp",EDGE,"E37")}),1.0]])]});
            var Q2;
            Q2=makeQuery(id+"F18.imprint","IMPRINT",FACE,{"disambiguationData":[TD([[makeQuery(id+"F18.imprint","IMPRINT",EDGE,{"derivedFrom":sQuery(id+"F18.wireOp",EDGE,"E36")}),1.0]])]});
            var Q3;
            Q3=makeQuery(id+"F18.imprint","IMPRINT",FACE,{"disambiguationData":[TD([[makeQuery(id+"F18.imprint","IMPRINT",EDGE,{"derivedFrom":sQuery(id+"F18.wireOp",EDGE,"E35")}),1.0]])]});
            var Q4;
            Q4=makeQuery(id+"F19.imprint","IMPRINT",FACE,{"disambiguationData":[TD([[makeQuery(id+"F19.imprint","IMPRINT",EDGE,{"derivedFrom":sQuery(id+"F19.wireOp",EDGE,"E47")}),1.0]])]});
            var Q5;
            Q5=makeQuery(id+"F19.imprint","IMPRINT",FACE,{"disambiguationData":[TD([[makeQuery(id+"F19.imprint","IMPRINT",EDGE,{"derivedFrom":sQuery(id+"F19.wireOp",EDGE,"E52")}),1.0]])]});
            extrude(context, id + "F23", {"entities" : qUnion([Q0, Q1, Q2, Q3, Q4, Q5]), "operationType" : NewBodyOperationType.REMOVE, "oppositeDirection" : true, "depth" : 25 * mm, "offsetDistance" : 25 * mm});
        }
        {
            var Q0;
            {var subQ3=sQuery(id+"F20.wireOp",EDGE,"E55.left");Q0=makeQuery(id+"F20.imprint","IMPRINT",FACE,{"disambiguationData":[TD([[makeQuery(id+"F20.imprint","IMPRINT",EDGE,{"derivedFrom":subQ3}),1.0]])]});}
            var Q1;
            {var subQ3=sQuery(id+"F20.wireOp",EDGE,"E56.left");Q1=makeQuery(id+"F20.imprint","IMPRINT",FACE,{"disambiguationData":[TD([[makeQuery(id+"F20.imprint","IMPRINT",EDGE,{"derivedFrom":subQ3}),1.0]])]});}
            var Q2;
            {var subQ3=sQuery(id+"F21.wireOp",EDGE,"E70.left");Q2=makeQuery(id+"F21.imprint","IMPRINT",FACE,{"disambiguationData":[TD([[makeQuery(id+"F21.imprint","IMPRINT",EDGE,{"derivedFrom":subQ3}),1.0]])]});}
            extrude(context, id + "F24", {"entities" : qUnion([Q0, Q1, Q2]), "operationType" : NewBodyOperationType.ADD, "depth" : 1 * mm, "offsetDistance" : 25 * mm});
        }
        {
            var Q0;
            Q0=makeQuery(id+"F21.imprint","IMPRINT",FACE,{"disambiguationData":[TD([[makeQuery(id+"F21.imprint","IMPRINT",EDGE,{"derivedFrom":sQuery(id+"F21.wireOp",EDGE,"E75")}),1.0]])]});
            var Q1;
            Q1=makeQuery(id+"F21.imprint","IMPRINT",FACE,{"disambiguationData":[TD([[makeQuery(id+"F21.imprint","IMPRINT",EDGE,{"derivedFrom":sQuery(id+"F21.wireOp",EDGE,"E80")}),1.0]])]});
            var Q2;
            Q2=makeQuery(id+"F20.imprint","IMPRINT",FACE,{"disambiguationData":[TD([[makeQuery(id+"F20.imprint","IMPRINT",EDGE,{"derivedFrom":sQuery(id+"F20.wireOp",EDGE,"E62")}),1.0]])]});
            var Q3;
            Q3=makeQuery(id+"F20.imprint","IMPRINT",FACE,{"disambiguationData":[TD([[makeQuery(id+"F20.imprint","IMPRINT",EDGE,{"derivedFrom":sQuery(id+"F20.wireOp",EDGE,"E65")}),1.0]])]});
            var Q4;
            Q4=makeQuery(id+"F20.imprint","IMPRINT",FACE,{"disambiguationData":[TD([[makeQuery(id+"F20.imprint","IMPRINT",EDGE,{"derivedFrom":sQuery(id+"F20.wireOp",EDGE,"E61")}),1.0]])]});
            var Q5;
            Q5=makeQuery(id+"F20.imprint","IMPRINT",FACE,{"disambiguationData":[TD([[makeQuery(id+"F20.imprint","IMPRINT",EDGE,{"derivedFrom":sQuery(id+"F20.wireOp",EDGE,"E66")}),1.0]])]});
            extrude(context, id + "F25", {"entities" : qUnion([Q0, Q1, Q2, Q3, Q4, Q5]), "operationType" : NewBodyOperationType.REMOVE, "depth" : 25 * mm, "offsetDistance" : 25 * mm});
        }
        {
            var Q0;
            Q0=makeQuery(id+"F22.opExtrude","CAP_EDGE",EDGE,{"disambiguationData":[OSD([sQuery(id+"F18.wireOp",EDGE,"E26.top")])],"isStart":false});
            var Q1;
            Q1=makeQuery(id+"F22.opExtrude","CAP_EDGE",EDGE,{"disambiguationData":[OSD([sQuery(id+"F18.wireOp",EDGE,"E26.bottom")])],"isStart":false});
            var Q2;
            Q2=makeQuery(id+"F22.opExtrude","CAP_EDGE",EDGE,{"disambiguationData":[OSD([sQuery(id+"F18.wireOp",EDGE,"E27.top")])],"isStart":false});
            var Q3;
            Q3=makeQuery(id+"F22.opExtrude","CAP_EDGE",EDGE,{"disambiguationData":[OSD([sQuery(id+"F18.wireOp",EDGE,"E27.bottom")])],"isStart":false});
            var Q4;
            Q4=makeQuery(id+"F22.opExtrude","CAP_EDGE",EDGE,{"disambiguationData":[OSD([sQuery(id+"F19.wireOp",EDGE,"E42.top")])],"isStart":false});
            var Q5;
            Q5=makeQuery(id+"F22.opExtrude","CAP_EDGE",EDGE,{"disambiguationData":[OSD([sQuery(id+"F19.wireOp",EDGE,"E42.bottom")])],"isStart":false});
            var Q6;
            Q6=makeQuery(id+"F24.opExtrude","CAP_EDGE",EDGE,{"disambiguationData":[OSD([sQuery(id+"F20.wireOp",EDGE,"E55.bottom")])],"isStart":false});
            var Q7;
            Q7=makeQuery(id+"F24.opExtrude","CAP_EDGE",EDGE,{"disambiguationData":[OSD([sQuery(id+"F20.wireOp",EDGE,"E56.bottom")])],"isStart":false});
            var Q8;
            Q8=makeQuery(id+"F24.opExtrude","CAP_EDGE",EDGE,{"disambiguationData":[OSD([sQuery(id+"F20.wireOp",EDGE,"E56.top")])],"isStart":false});
            var Q9;
            Q9=makeQuery(id+"F24.opExtrude","CAP_EDGE",EDGE,{"disambiguationData":[OSD([sQuery(id+"F20.wireOp",EDGE,"E55.top")])],"isStart":false});
            var Q10;
            Q10=makeQuery(id+"F24.opExtrude","CAP_EDGE",EDGE,{"disambiguationData":[OSD([sQuery(id+"F21.wireOp",EDGE,"E70.top")])],"isStart":false});
            var Q11;
            Q11=makeQuery(id+"F24.opExtrude","CAP_EDGE",EDGE,{"disambiguationData":[OSD([sQuery(id+"F21.wireOp",EDGE,"E70.bottom")])],"isStart":false});
            fillet(context, id + "F26", {"entities" : qUnion([Q0, Q1, Q2, Q3, Q4, Q5, Q6, Q7, Q8, Q9, Q10, Q11]), "radius" : 1 * mm, "tangentPropagation" : true, "allowEdgeOverflow" : false});
        }
        {
            var Q0;
            Q0=makeQuery(id+"F3.opExtrude","SWEPT_FACE",FACE,{"disambiguationData":[OSD([sQuery(id+"F0.wireOp",EDGE,"E23")])]});
            var sketch = newSketch(context, id + "F27", { "sketchPlane" : qUnion([Q0])});
            skLineSegment(sketch, "E81.bottom", {"start": v(27.5, 2.5) * mm, "end": v(37.5, 2.5) * mm});
            skLineSegment(sketch, "E81.top", {"start": v(27.5, 0) * mm, "end": v(37.5, 0) * mm});
            skLineSegment(sketch, "E81.left", {"start": v(27.5, 2.5) * mm, "end": v(27.5, 0) * mm});
            skLineSegment(sketch, "E81.right", {"start": v(37.5, 2.5) * mm, "end": v(37.5, 0) * mm});
            skSolve(sketch);
        }
        {
            var Q0;
            Q0=makeQuery(id+"F27.imprint","IMPRINT",FACE,{"disambiguationData":[TD([[makeQuery(id+"F27.imprint","IMPRINT",EDGE,{"derivedFrom":sQuery(id+"F27.wireOp",EDGE,"E81.bottom")}),-1.0]])]});
            extrude(context, id + "F28", {"entities" : qUnion([Q0]), "operationType" : NewBodyOperationType.REMOVE, "oppositeDirection" : true, "depth" : 15 * mm, "offsetDistance" : 25 * mm});
        }
    });
